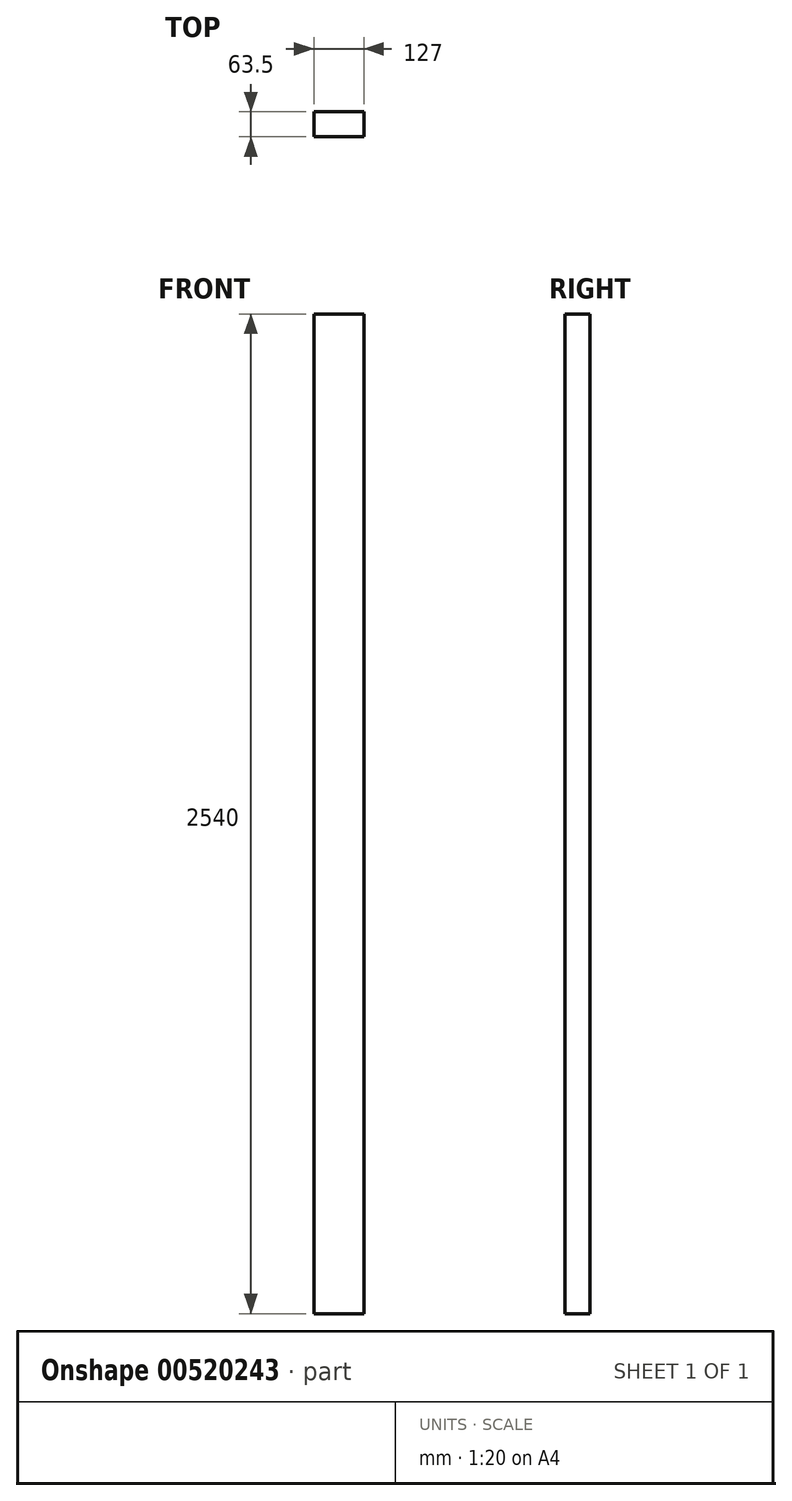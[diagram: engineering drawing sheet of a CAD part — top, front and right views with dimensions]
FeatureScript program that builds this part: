
annotation { "Feature Type Name" : "Feature", "Feature Type Description" : "" }
export const myFeature = defineFeature(function(context is Context, id is Id, definition is map)
    precondition{}
    {
        {
            var Q0;
            Q0=qCreatedBy(makeId("Top.planeOp"),FACE);
            var sketch = newSketch(context, id + "F0", { "sketchPlane" : qUnion([Q0])});
            skLineSegment(sketch, "E0.bottom", {"start": v(-54.76, 35.57) * mm, "end": v(72.24, 35.57) * mm});
            skLineSegment(sketch, "E0.top", {"start": v(-54.76, -27.93) * mm, "end": v(72.24, -27.93) * mm});
            skLineSegment(sketch, "E0.left", {"start": v(-54.76, 35.57) * mm, "end": v(-54.76, -27.93) * mm});
            skLineSegment(sketch, "E0.right", {"start": v(72.24, 35.57) * mm, "end": v(72.24, -27.93) * mm});
            skSolve(sketch);
        }
        {
            var Q0;
            Q0 = qSketchRegion(id + "F0", true);
            extrude(context, id + "F1", {"entities" : qUnion([Q0]), "depth" : 2540 * mm, "offsetDistance" : 25.4 * mm});
        }
    });
